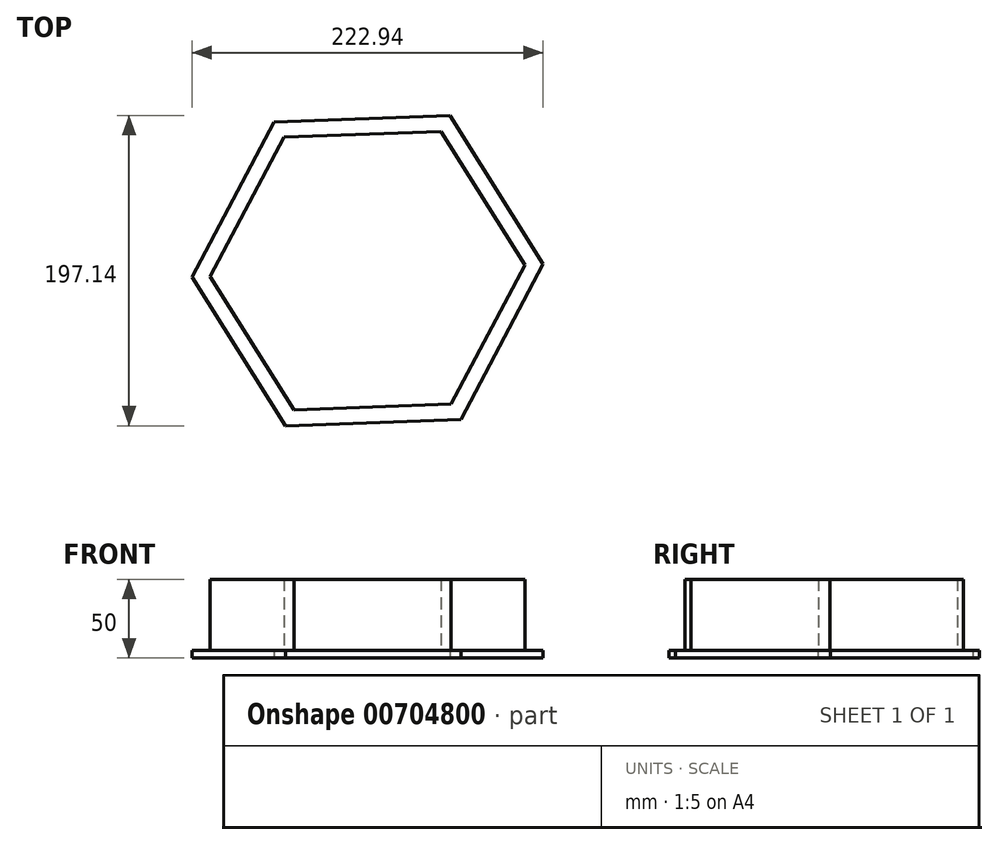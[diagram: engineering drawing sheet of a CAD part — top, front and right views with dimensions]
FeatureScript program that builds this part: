
annotation { "Feature Type Name" : "Feature", "Feature Type Description" : "" }
export const myFeature = defineFeature(function(context is Context, id is Id, definition is map)
    precondition{}
    {
        {
            var Q0;
            Q0=qCreatedBy(makeId("Top.planeOp"),FACE);
            var sketch = newSketch(context, id + "F0", { "sketchPlane" : qUnion([Q0])});
            skCircle(sketch, "E0.cCircle", {"center": v(0, 0) * mm, "radius": 86.6 * mm, "construction": true});
            skLineSegment(sketch, "E0.0", {"start": v(99.93, 3.64) * mm, "end": v(53.12, -84.72) * mm});
            skLineSegment(sketch, "E0.1", {"start": v(53.12, -84.72) * mm, "end": v(-46.81, -88.37) * mm});
            skLineSegment(sketch, "E0.2", {"start": v(-46.81, -88.37) * mm, "end": v(-99.93, -3.64) * mm});
            skLineSegment(sketch, "E0.3", {"start": v(-99.93, -3.64) * mm, "end": v(-53.12, 84.72) * mm});
            skLineSegment(sketch, "E0.4", {"start": v(-53.12, 84.72) * mm, "end": v(46.81, 88.37) * mm});
            skLineSegment(sketch, "E0.5", {"start": v(46.81, 88.37) * mm, "end": v(99.93, 3.64) * mm});
            skPoint(sketch, "E0.0.midPoint", {"position": v(76.53, -40.54) * mm});
            skSolve(sketch);
        }
        {
            var Q0;
            Q0=makeQuery(id+"F0.imprint","IMPRINT",FACE,{"disambiguationData":[TD([[makeQuery(id+"F0.imprint","IMPRINT",EDGE,{"derivedFrom":sQuery(id+"F0.wireOp",EDGE,"E0.0")}),-1.0]])]});
            extrude(context, id + "F1", {"entities" : qUnion([Q0]), "depth" : 50 * mm, "offsetDistance" : 25.4 * mm});
        }
        {
            var Q0;
            Q0=makeQuery(id+"F0.imprint","IMPRINT",FACE,{"disambiguationData":[TD([[makeQuery(id+"F0.imprint","IMPRINT",EDGE,{"derivedFrom":sQuery(id+"F0.wireOp",EDGE,"E0.0")}),-1.0]])]});
            var sketch = newSketch(context, id + "F2", { "sketchPlane" : qUnion([Q0])});
            skLineSegment(sketch, "E1.0", {"start": v(59.26, -94.5) * mm, "end": v(111.47, 4.06) * mm});
            skLineSegment(sketch, "E1.1", {"start": v(52.22, 98.57) * mm, "end": v(-59.26, 94.5) * mm});
            skLineSegment(sketch, "E1.2", {"start": v(-59.26, 94.5) * mm, "end": v(-111.47, -4.06) * mm});
            skLineSegment(sketch, "E1.3", {"start": v(111.47, 4.06) * mm, "end": v(52.22, 98.57) * mm});
            skLineSegment(sketch, "E1.4", {"start": v(-111.47, -4.06) * mm, "end": v(-52.22, -98.57) * mm});
            skLineSegment(sketch, "E1.5", {"start": v(-52.22, -98.57) * mm, "end": v(59.26, -94.5) * mm});
            skSolve(sketch);
        }
        {
            var Q0;
            Q0=makeQuery(id+"F2.imprint","IMPRINT",FACE,{"disambiguationData":[TD([[makeQuery(id+"F2.imprint","IMPRINT",EDGE,{"derivedFrom":sQuery(id+"F2.wireOp",EDGE,"E1.0")}),1.0]])]});
            extrude(context, id + "F3", {"entities" : qUnion([Q0]), "operationType" : NewBodyOperationType.ADD, "depth" : 5 * mm, "offsetDistance" : 25 * mm});
        }
    });
